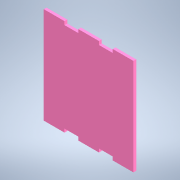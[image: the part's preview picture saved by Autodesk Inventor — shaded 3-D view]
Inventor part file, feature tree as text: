
AUTODESK INVENTOR PART (.ipt)
format: ipt  version: 2020.3 (Build 243373000, 373)  size: 126,976 bytes
history: native  units: mm
features: projected_geometry x5, sketch x2, extrude x1
ambient origin geometry x8: Origin, YZ Plane, XZ Plane, XY Plane, X Axis, Y Axis, Z Axis, Center Point
bodies: Solid1 (feature_tree)
feature tree (8):
  extrude  "Extrusion1"  [1 undecoded]
  sketch  "Sketch2"
  sketch  "Sketch1"  dims[d5=4.0mm d6=0.0mm]
  projected_geometry  "Projected Loop1"
  projected_geometry  "Projected Loop2"
  projected_geometry  "Projected Loop3"
  projected_geometry  "Projected Loop4"
  projected_geometry  "Projected Loop5"
note: 1 required parameter value undecoded (feature->parameter linkage not recoverable at this tier; creation-order binding heuristic only, values carry confidence <= 0.55)
